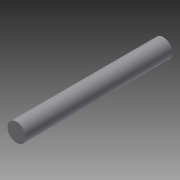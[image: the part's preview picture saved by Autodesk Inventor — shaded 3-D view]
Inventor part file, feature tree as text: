
AUTODESK INVENTOR PART (.ipt)
format: ipt  version: 2013 (Build 170138000, 138)  size: 67,584 bytes
history: native  units: in
note: dims shown in document units (in); Inventor stores cm internally (conversion verified against a paired STEP export)
features: extrude x1, sketch x1
ambient origin geometry x8: Origin, YZ Plane, XZ Plane, XY Plane, X Axis, Y Axis, Z Axis, Center Point
bodies: Solid1 (feature_tree)
feature tree (2):
  extrude  "Extrusion1"  Depth=1.5in TaperAngle=0.0deg
  sketch  "Sketch1"  dims[d0=0.1875in d1=1.5in d2=0.0in]
